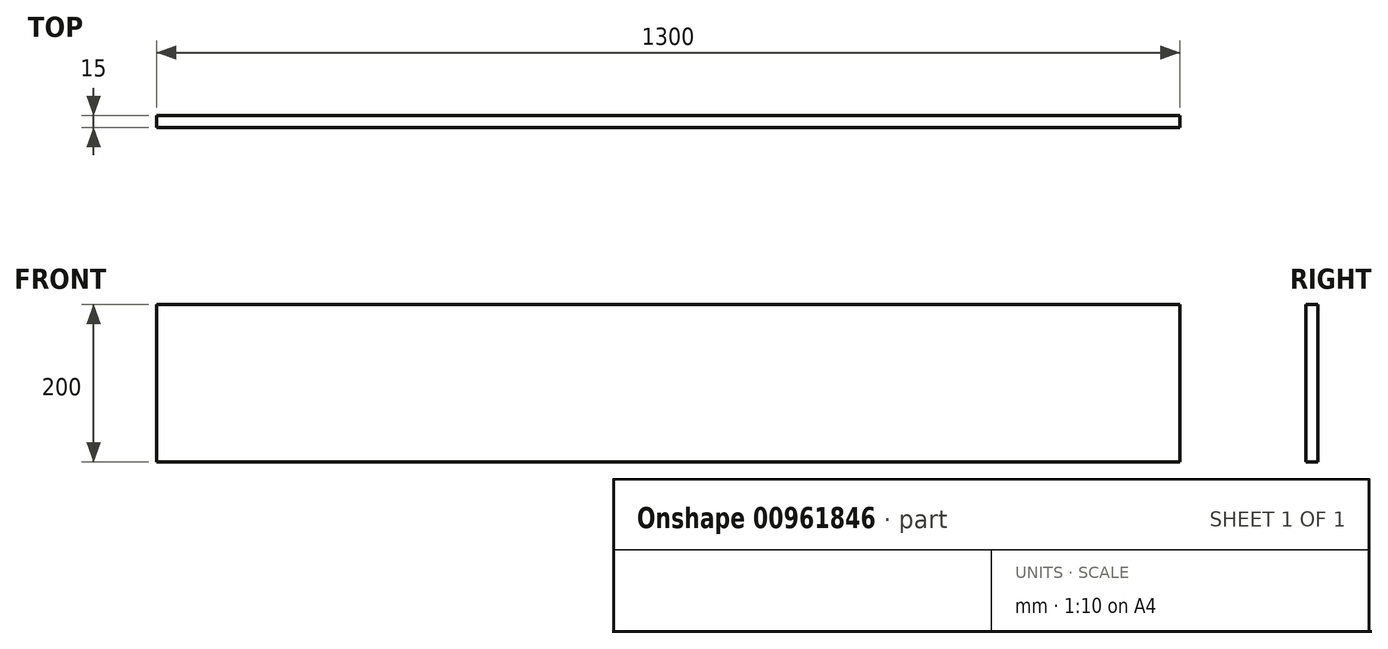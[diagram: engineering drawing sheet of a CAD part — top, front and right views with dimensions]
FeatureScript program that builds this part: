
annotation { "Feature Type Name" : "Feature", "Feature Type Description" : "" }
export const myFeature = defineFeature(function(context is Context, id is Id, definition is map)
    precondition{}
    {
        {
            var Q0;
            Q0=qCreatedBy(makeId("Front.planeOp"),FACE);
            var sketch = newSketch(context, id + "F0", { "sketchPlane" : qUnion([Q0])});
            skLineSegment(sketch, "E0.bottom", {"start": v(0, 0) * mm, "end": v(1300, 0) * mm});
            skLineSegment(sketch, "E0.top", {"start": v(0, 200) * mm, "end": v(1300, 200) * mm});
            skLineSegment(sketch, "E0.left", {"start": v(0, 0) * mm, "end": v(0, 200) * mm});
            skLineSegment(sketch, "E0.right", {"start": v(1300, 0) * mm, "end": v(1300, 200) * mm});
            skSolve(sketch);
        }
        {
            var Q0;
            Q0=makeQuery(id+"F0.imprint","IMPRINT",FACE,{"disambiguationData":[TD([[makeQuery(id+"F0.imprint","IMPRINT",EDGE,{"derivedFrom":sQuery(id+"F0.wireOp",EDGE,"E0.bottom")}),1.0]])]});
            extrude(context, id + "F1", {"entities" : qUnion([Q0]), "depth" : 15 * mm, "offsetDistance" : 25.4 * mm});
        }
    });
